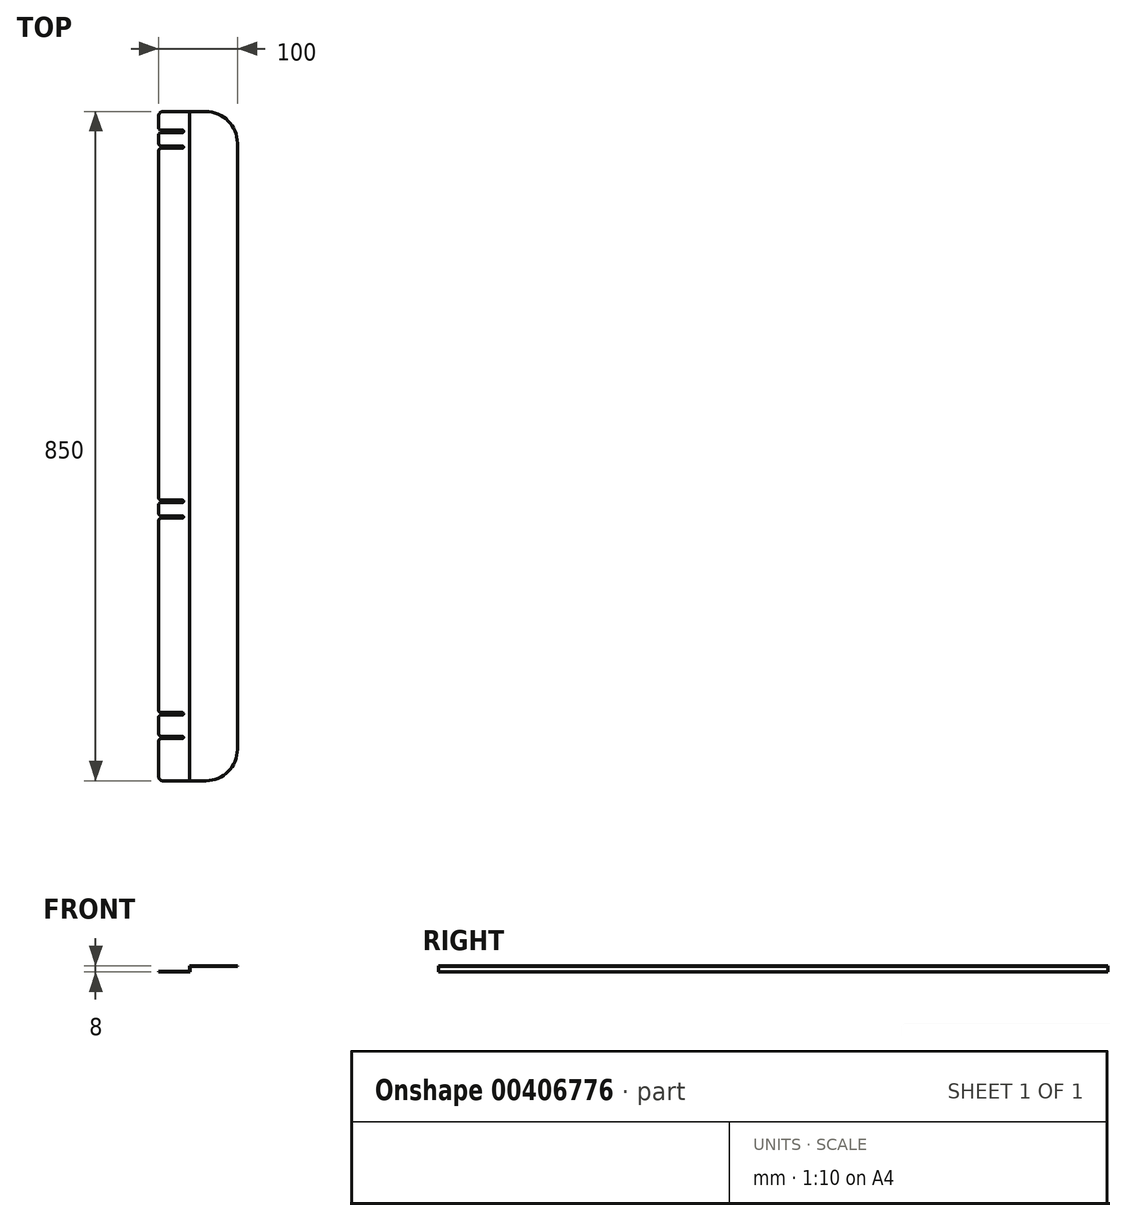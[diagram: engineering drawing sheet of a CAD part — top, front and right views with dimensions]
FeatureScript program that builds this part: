
annotation { "Feature Type Name" : "Feature", "Feature Type Description" : "" }
export const myFeature = defineFeature(function(context is Context, id is Id, definition is map)
    precondition{}
    {
        {
            var Q0;
            Q0=qCreatedBy(makeId("Top.planeOp"),FACE);
            var sketch = newSketch(context, id + "F0", { "sketchPlane" : qUnion([Q0])});
            skLineSegment(sketch, "E0.bottom", {"start": v(-95, 795) * mm, "end": v(-40, 795) * mm});
            skLineSegment(sketch, "E0.top", {"start": v(-95, -55) * mm, "end": v(-40, -55) * mm});
            skLineSegment(sketch, "E0.left", {"start": v(-100, 790) * mm, "end": v(-100, -50) * mm});
            skLineSegment(sketch, "E0.right", {"start": v(0, 755) * mm, "end": v(0, -15) * mm});
            skCircle(sketch, "E1", {"center": v(-70, 770) * mm, "radius": 1.5 * mm});
            skCircle(sketch, "E2", {"center": v(-70, 750) * mm, "radius": 1.5 * mm});
            skCircle(sketch, "E3", {"center": v(-70, 300) * mm, "radius": 1.5 * mm});
            skCircle(sketch, "E4", {"center": v(-70, 280) * mm, "radius": 1.5 * mm});
            skCircle(sketch, "E5", {"center": v(-70, 30) * mm, "radius": 1.5 * mm});
            skCircle(sketch, "E6", {"center": v(-70, 0) * mm, "radius": 1.5 * mm});
            skLineSegment(sketch, "E7", {"start": v(-70, 795) * mm, "end": v(-70, -55) * mm, "construction": true});
            skLineSegment(sketch, "E8.bottom", {"start": v(141.58, 735) * mm, "end": v(-337.65, 735) * mm, "construction": true});
            skLineSegment(sketch, "E8.top", {"start": v(141.58, 345) * mm, "end": v(-337.65, 345) * mm, "construction": true});
            skLineSegment(sketch, "E8.left", {"start": v(141.58, 735) * mm, "end": v(141.58, 345) * mm, "construction": true});
            skLineSegment(sketch, "E8.right", {"start": v(-337.65, 735) * mm, "end": v(-337.65, 345) * mm, "construction": true});
            skPoint(sketch, "E9.visualSharp", {"position": v(0, -55) * mm});
            skArc(sketch, "E9.filletArc", {"start": v(-40, -55) * mm, "mid": v(-11.72, -43.28) * mm, "end": v(0, -15) * mm});
            skPoint(sketch, "E10.visualSharp", {"position": v(0, 795) * mm});
            skArc(sketch, "E10.filletArc", {"start": v(0, 755) * mm, "mid": v(-11.72, 783.28) * mm, "end": v(-40, 795) * mm});
            skPoint(sketch, "E11.visualSharp", {"position": v(-100, -55) * mm});
            skArc(sketch, "E11.filletArc", {"start": v(-100, -50) * mm, "mid": v(-98.54, -53.54) * mm, "end": v(-95, -55) * mm});
            skPoint(sketch, "E12.visualSharp", {"position": v(-100, 795) * mm});
            skArc(sketch, "E12.filletArc", {"start": v(-95, 795) * mm, "mid": v(-98.54, 793.54) * mm, "end": v(-100, 790) * mm});
            skLineSegment(sketch, "E13.bottom", {"start": v(-70, 751.5) * mm, "end": v(-100, 751.5) * mm});
            skLineSegment(sketch, "E13.top", {"start": v(-70, 748.5) * mm, "end": v(-100, 748.5) * mm});
            skLineSegment(sketch, "E13.left", {"start": v(-70, 751.5) * mm, "end": v(-70, 748.5) * mm});
            skLineSegment(sketch, "E13.right", {"start": v(-100, 751.5) * mm, "end": v(-100, 748.5) * mm});
            skLineSegment(sketch, "E14.bottom", {"start": v(-70, 771.5) * mm, "end": v(-100, 771.5) * mm});
            skLineSegment(sketch, "E14.top", {"start": v(-70, 768.5) * mm, "end": v(-100, 768.5) * mm});
            skLineSegment(sketch, "E14.left", {"start": v(-70, 771.5) * mm, "end": v(-70, 768.5) * mm});
            skLineSegment(sketch, "E14.right", {"start": v(-100, 771.5) * mm, "end": v(-100, 768.5) * mm});
            skLineSegment(sketch, "E15.bottom", {"start": v(-70, 301.5) * mm, "end": v(-100, 301.5) * mm});
            skLineSegment(sketch, "E15.top", {"start": v(-70, 298.5) * mm, "end": v(-100, 298.5) * mm});
            skLineSegment(sketch, "E15.left", {"start": v(-70, 301.5) * mm, "end": v(-70, 298.5) * mm});
            skLineSegment(sketch, "E15.right", {"start": v(-100, 301.5) * mm, "end": v(-100, 298.5) * mm});
            skLineSegment(sketch, "E16.bottom", {"start": v(-70, 281.5) * mm, "end": v(-100, 281.5) * mm});
            skLineSegment(sketch, "E16.top", {"start": v(-70, 278.5) * mm, "end": v(-100, 278.5) * mm});
            skLineSegment(sketch, "E16.left", {"start": v(-70, 281.5) * mm, "end": v(-70, 278.5) * mm});
            skLineSegment(sketch, "E16.right", {"start": v(-100, 281.5) * mm, "end": v(-100, 278.5) * mm});
            skLineSegment(sketch, "E17.bottom", {"start": v(-70, 31.5) * mm, "end": v(-100, 31.5) * mm});
            skLineSegment(sketch, "E17.top", {"start": v(-70, 28.5) * mm, "end": v(-100, 28.5) * mm});
            skLineSegment(sketch, "E17.left", {"start": v(-70, 31.5) * mm, "end": v(-70, 28.5) * mm});
            skLineSegment(sketch, "E17.right", {"start": v(-100, 31.5) * mm, "end": v(-100, 28.5) * mm});
            skLineSegment(sketch, "E18.bottom", {"start": v(-70, 1.5) * mm, "end": v(-100, 1.5) * mm});
            skLineSegment(sketch, "E18.top", {"start": v(-70, -1.5) * mm, "end": v(-100, -1.5) * mm});
            skLineSegment(sketch, "E18.left", {"start": v(-70, 1.5) * mm, "end": v(-70, -1.5) * mm});
            skLineSegment(sketch, "E18.right", {"start": v(-100, 1.5) * mm, "end": v(-100, -1.5) * mm});
            skSolve(sketch);
        }
        {
            var Q0;
            Q0=makeQuery(id+"F0.imprint","IMPRINT",FACE,{"disambiguationData":[TD([[makeQuery(id+"F0.imprint","IMPRINT",EDGE,{"derivedFrom":sQuery(id+"F0.wireOp",EDGE,"E0.bottom")}),-1.0]])]});
            extrude(context, id + "F1", {"entities" : qUnion([Q0]), "depth" : 8 * mm});
        }
        {
            var Q0;
            Q0=makeQuery(id+"F1.opExtrude","SWEPT_EDGE",EDGE,{"disambiguationData":[OSD([sQuery(id+"F0.wireOp",EDGE,"E0.left"),sQuery(id+"F0.wireOp",EDGE,"E14.bottom"),sQuery(id+"F0.wireOp",EDGE,"E14.right")])]});
            var Q1;
            Q1=makeQuery(id+"F1.opExtrude","SWEPT_EDGE",EDGE,{"disambiguationData":[OSD([sQuery(id+"F0.wireOp",EDGE,"E0.left"),sQuery(id+"F0.wireOp",EDGE,"E14.top"),sQuery(id+"F0.wireOp",EDGE,"E14.right")])]});
            var Q2;
            Q2=makeQuery(id+"F1.opExtrude","SWEPT_EDGE",EDGE,{"disambiguationData":[OSD([sQuery(id+"F0.wireOp",EDGE,"E0.left"),sQuery(id+"F0.wireOp",EDGE,"E13.bottom"),sQuery(id+"F0.wireOp",EDGE,"E13.right")])]});
            var Q3;
            Q3=makeQuery(id+"F1.opExtrude","SWEPT_EDGE",EDGE,{"disambiguationData":[OSD([sQuery(id+"F0.wireOp",EDGE,"E0.left"),sQuery(id+"F0.wireOp",EDGE,"E13.top"),sQuery(id+"F0.wireOp",EDGE,"E13.right")])]});
            var Q4;
            Q4=makeQuery(id+"F1.opExtrude","SWEPT_EDGE",EDGE,{"disambiguationData":[OSD([sQuery(id+"F0.wireOp",EDGE,"E0.left"),sQuery(id+"F0.wireOp",EDGE,"E15.bottom"),sQuery(id+"F0.wireOp",EDGE,"E15.right")])]});
            var Q5;
            Q5=makeQuery(id+"F1.opExtrude","SWEPT_EDGE",EDGE,{"disambiguationData":[OSD([sQuery(id+"F0.wireOp",EDGE,"E0.left"),sQuery(id+"F0.wireOp",EDGE,"E15.top"),sQuery(id+"F0.wireOp",EDGE,"E15.right")])]});
            var Q6;
            Q6=makeQuery(id+"F1.opExtrude","SWEPT_EDGE",EDGE,{"disambiguationData":[OSD([sQuery(id+"F0.wireOp",EDGE,"E0.left"),sQuery(id+"F0.wireOp",EDGE,"E16.bottom"),sQuery(id+"F0.wireOp",EDGE,"E16.right")])]});
            var Q7;
            Q7=makeQuery(id+"F1.opExtrude","SWEPT_EDGE",EDGE,{"disambiguationData":[OSD([sQuery(id+"F0.wireOp",EDGE,"E0.left"),sQuery(id+"F0.wireOp",EDGE,"E16.top"),sQuery(id+"F0.wireOp",EDGE,"E16.right")])]});
            var Q8;
            Q8=makeQuery(id+"F1.opExtrude","SWEPT_EDGE",EDGE,{"disambiguationData":[OSD([sQuery(id+"F0.wireOp",EDGE,"E0.left"),sQuery(id+"F0.wireOp",EDGE,"E17.bottom"),sQuery(id+"F0.wireOp",EDGE,"E17.right")])]});
            var Q9;
            Q9=makeQuery(id+"F1.opExtrude","SWEPT_EDGE",EDGE,{"disambiguationData":[OSD([sQuery(id+"F0.wireOp",EDGE,"E0.left"),sQuery(id+"F0.wireOp",EDGE,"E17.top"),sQuery(id+"F0.wireOp",EDGE,"E17.right")])]});
            var Q10;
            Q10=makeQuery(id+"F1.opExtrude","SWEPT_EDGE",EDGE,{"disambiguationData":[OSD([sQuery(id+"F0.wireOp",EDGE,"E0.left"),sQuery(id+"F0.wireOp",EDGE,"E18.bottom"),sQuery(id+"F0.wireOp",EDGE,"E18.right")])]});
            var Q11;
            Q11=makeQuery(id+"F1.opExtrude","SWEPT_EDGE",EDGE,{"disambiguationData":[OSD([sQuery(id+"F0.wireOp",EDGE,"E0.left"),sQuery(id+"F0.wireOp",EDGE,"E18.top"),sQuery(id+"F0.wireOp",EDGE,"E18.right")])]});
            fillet(context, id + "F2", {"entities" : qUnion([Q0, Q1, Q2, Q3, Q4, Q5, Q6, Q7, Q8, Q9, Q10, Q11]), "radius" : 3 * mm, "tangentPropagation" : true, "allowEdgeOverflow" : false});
        }
        {
            var Q0;
            Q0=makeQuery(id+"F1.opExtrude","SWEPT_FACE",FACE,{"disambiguationData":[OSD([sQuery(id+"F0.wireOp",EDGE,"E0.top")])]});
            var sketch = newSketch(context, id + "F3", { "sketchPlane" : qUnion([Q0])});
            skLineSegment(sketch, "E19.bottom", {"start": v(-120, 8) * mm, "end": v(0, 8) * mm});
            skLineSegment(sketch, "E19.top", {"start": v(-120, 0) * mm, "end": v(0, 0) * mm});
            skLineSegment(sketch, "E19.left", {"start": v(-120, 8) * mm, "end": v(-120, 0) * mm});
            skLineSegment(sketch, "E19.right", {"start": v(0, 8) * mm, "end": v(0, 0) * mm});
            skLineSegment(sketch, "E20", {"start": v(0, 7) * mm, "end": v(-60, 7) * mm});
            skLineSegment(sketch, "E21", {"start": v(-60, 7) * mm, "end": v(-60, 1) * mm});
            skLineSegment(sketch, "E22", {"start": v(-60, 1) * mm, "end": v(-120, 1) * mm});
            skLineSegment(sketch, "E23", {"start": v(-61, 8) * mm, "end": v(-61, 1) * mm});
            skLineSegment(sketch, "E24", {"start": v(-60, 1) * mm, "end": v(-60, 0) * mm});
            skSolve(sketch);
        }
        {
            var Q0;
            {var subQ1=sQuery(id+"F3.wireOp",EDGE,"E21");Q0=makeQuery(id+"F3.imprint","IMPRINT",FACE,{"disambiguationData":[TD([[makeQuery(id+"F3.imprint","IMPRINT",EDGE,{"derivedFrom":subQ1}),1.0]])]});}
            var Q1;
            {var subQ0=sQuery(id+"F3.wireOp",EDGE,"E19.top");var subQ3=sQuery(id+"F3.wireOp",EDGE,"E19.right");var subQ4=makeQuery(id+"F3.imprint","INTERSECT",VERTEX,{"derivedFrom":[subQ0,subQ3]});Q1=makeQuery(id+"F3.imprint","IMPRINT",FACE,{"disambiguationData":[TD([[makeQuery(id+"F3.imprint","IMPRINT",EDGE,{"disambiguationData":[TD([[subQ4,1.0]])],"derivedFrom":subQ3}),-1.0]])]});}
            var Q2;
            {var subQ3=sQuery(id+"F3.wireOp",EDGE,"E23");Q2=makeQuery(id+"F3.imprint","IMPRINT",FACE,{"disambiguationData":[TD([[makeQuery(id+"F3.imprint","IMPRINT",EDGE,{"derivedFrom":subQ3}),-1.0]])]});}
            var Q3;
            {var subQ0=sQuery(id+"F3.wireOp",EDGE,"E19.bottom");var subQ3=sQuery(id+"F3.wireOp",EDGE,"E19.left");var subQ4=makeQuery(id+"F3.imprint","INTERSECT",VERTEX,{"derivedFrom":[subQ0,subQ3]});Q3=makeQuery(id+"F3.imprint","IMPRINT",FACE,{"disambiguationData":[TD([[makeQuery(id+"F3.imprint","IMPRINT",EDGE,{"disambiguationData":[TD([[subQ4,-1.0]])],"derivedFrom":subQ3}),1.0]])]});}
            extrude(context, id + "F4", {"entities" : qUnion([Q0, Q1, Q2, Q3]), "operationType" : NewBodyOperationType.REMOVE, "oppositeDirection" : true, "depth" : 1039 * mm});
        }
    });
